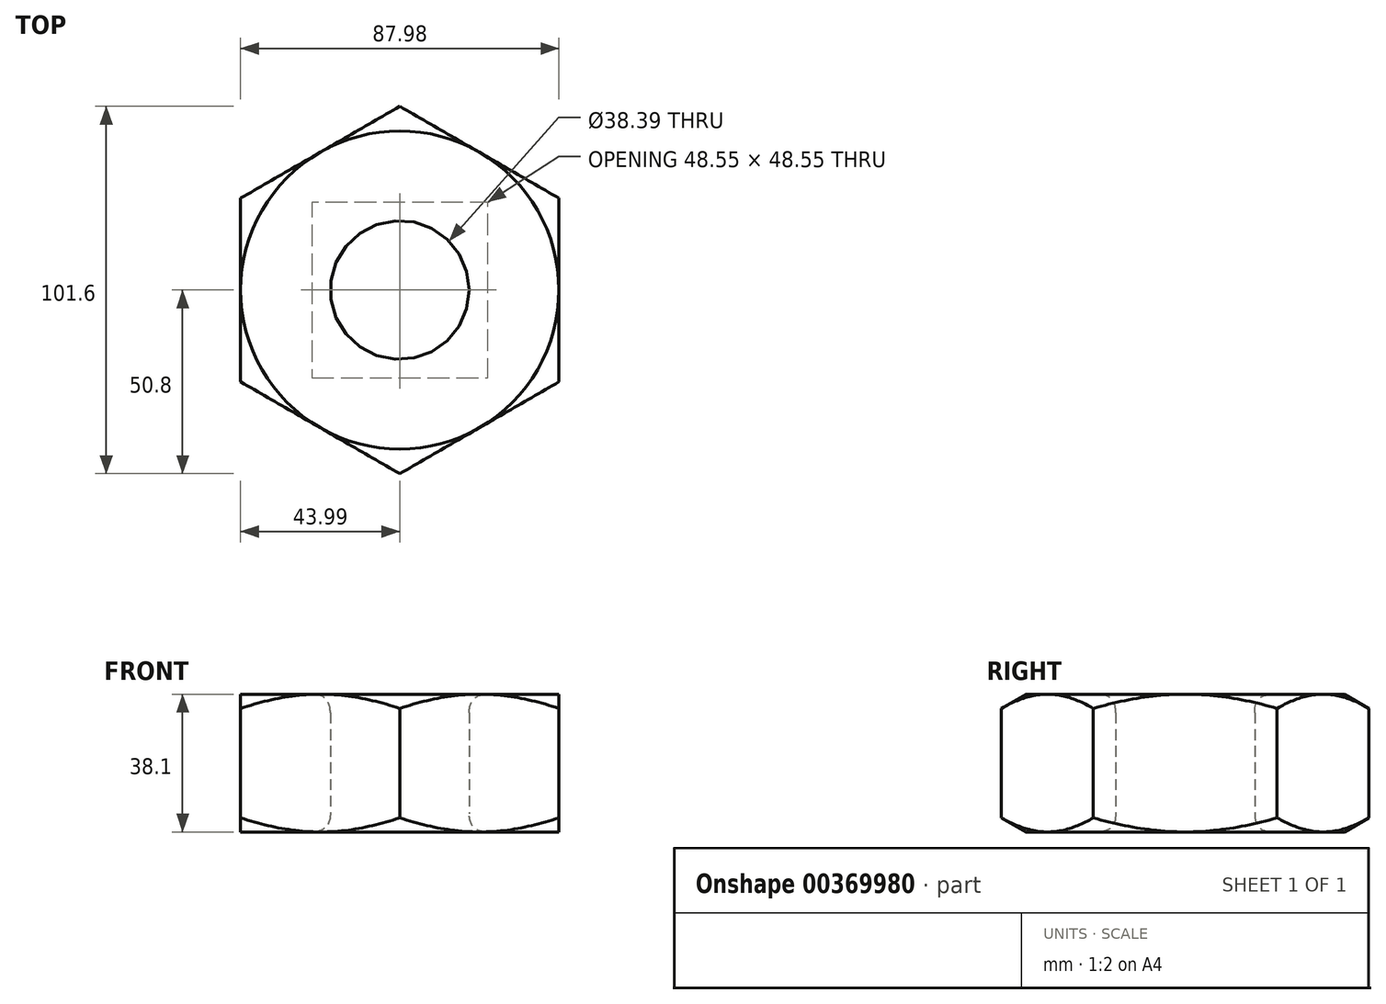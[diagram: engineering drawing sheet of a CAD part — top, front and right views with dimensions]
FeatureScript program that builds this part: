
annotation { "Feature Type Name" : "Feature", "Feature Type Description" : "" }
export const myFeature = defineFeature(function(context is Context, id is Id, definition is map)
    precondition{}
    {
        {
            var Q0;
            Q0=qCreatedBy(makeId("Top.planeOp"),FACE);
            var sketch = newSketch(context, id + "F0", { "sketchPlane" : qUnion([Q0])});
            skCircle(sketch, "E0.cCircle", {"center": v(0, 0) * mm, "radius": 44 * mm, "construction": true});
            skLineSegment(sketch, "E0.0", {"start": v(0, 50.8) * mm, "end": v(44, 25.4) * mm});
            skLineSegment(sketch, "E0.1", {"start": v(44, 25.4) * mm, "end": v(44, -25.4) * mm});
            skLineSegment(sketch, "E0.2", {"start": v(44, -25.4) * mm, "end": v(0, -50.8) * mm});
            skLineSegment(sketch, "E0.3", {"start": v(0, -50.8) * mm, "end": v(-44, -25.4) * mm});
            skLineSegment(sketch, "E0.4", {"start": v(-44, -25.4) * mm, "end": v(-44, 25.4) * mm});
            skLineSegment(sketch, "E0.5", {"start": v(-44, 25.4) * mm, "end": v(0, 50.8) * mm});
            skPoint(sketch, "E0.0.midPoint", {"position": v(22, 38.1) * mm});
            skCircle(sketch, "E1", {"center": v(0, 0) * mm, "radius": 19.2 * mm});
            skSolve(sketch);
        }
        {
            var Q0;
            Q0 = qSketchRegion(id + "F0", true);
            extrude(context, id + "F1", {"entities" : qUnion([Q0]), "depth" : 38.1 * mm});
        }
        {
            var Q0;
            Q0=qCreatedBy(makeId("Front.planeOp"),FACE);
            var sketch = newSketch(context, id + "F2", { "sketchPlane" : qUnion([Q0])});
            skLineSegment(sketch, "E2", {"start": v(0, 0) * mm, "end": v(0, 38.1) * mm, "construction": true});
            skLineSegment(sketch, "E3", {"start": v(0, 38.1) * mm, "end": v(0, 19.05) * mm, "construction": true});
            skLineSegment(sketch, "E4", {"start": v(0, 19.05) * mm, "end": v(44, 19.05) * mm, "construction": true});
            skLineSegment(sketch, "E5", {"start": v(66.43, 25.15) * mm, "end": v(66.43, 38.1) * mm});
            skLineSegment(sketch, "E6", {"start": v(66.43, 38.1) * mm, "end": v(44, 38.1) * mm});
            skLineSegment(sketch, "E7", {"start": v(44, 38.1) * mm, "end": v(66.43, 25.15) * mm});
            skLineSegment(sketch, "E8.MirrorCS", {"start": v(44, 0) * mm, "end": v(66.43, 12.95) * mm});
            skLineSegment(sketch, "E9.MirrorCS", {"start": v(66.43, 0) * mm, "end": v(44, 0) * mm});
            skLineSegment(sketch, "E10.MirrorCS", {"start": v(66.43, 12.95) * mm, "end": v(66.43, 0) * mm});
            skSolve(sketch);
        }
        {
            var Q0;
            Q0 = qSketchRegion(id + "F2", true);
            var Q1;
            Q1=sQuery(id+"F2.wireOp",EDGE,"E3");
            revolve(context, id + "F3", {"operationType" : NewBodyOperationType.REMOVE, "entities" : qUnion([Q0]), "axis" : qUnion([Q1]), "revolveType" : RevolveType.FULL, "oppositeDirection" : true});
        }
        {
            var Q0;
            Q0=makeQuery(id+"F1.opExtrude","SWEPT_FACE",FACE,{"disambiguationData":[OSD([sQuery(id+"F0.wireOp",EDGE,"E1")])]});
            fillet(context, id + "F4", {"entities" : qUnion([Q0]), "radius" : 5.08 * mm, "rho" : 0.5, "crossSection" : FilletCrossSection.CONIC, "allowEdgeOverflow" : false});
        }
    });
